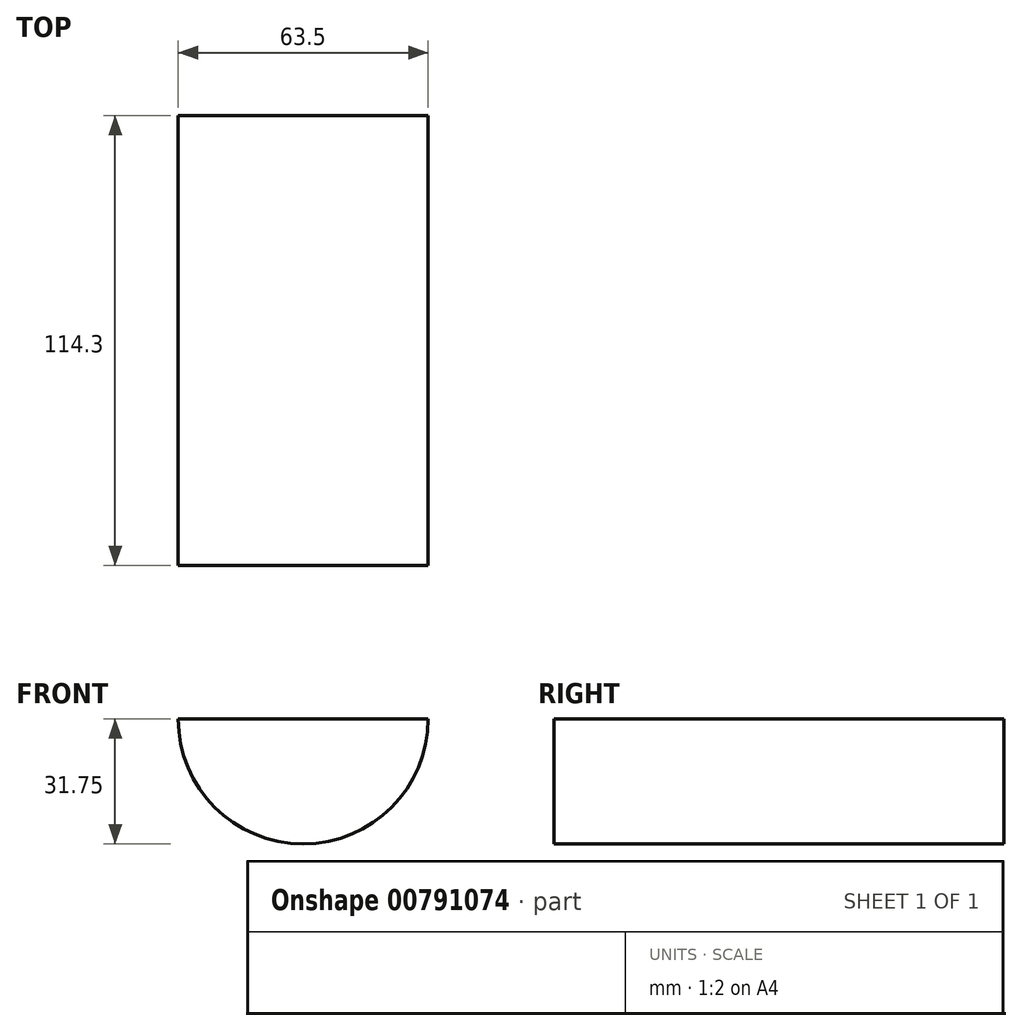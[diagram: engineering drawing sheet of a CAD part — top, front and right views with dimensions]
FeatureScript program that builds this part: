
annotation { "Feature Type Name" : "Feature", "Feature Type Description" : "" }
export const myFeature = defineFeature(function(context is Context, id is Id, definition is map)
    precondition{}
    {
        {
            var Q0;
            Q0=qCreatedBy(makeId("Front.planeOp"),FACE);
            var sketch = newSketch(context, id + "F0", { "sketchPlane" : qUnion([Q0])});
            skLineSegment(sketch, "E0", {"start": v(0, 0) * mm, "end": v(152.4, 0) * mm});
            skLineSegment(sketch, "E1", {"start": v(152.4, 0) * mm, "end": v(152.4, 92.08) * mm});
            skLineSegment(sketch, "E2", {"start": v(152.4, 92.08) * mm, "end": v(0, 92.08) * mm});
            skLineSegment(sketch, "E3", {"start": v(0, 92.08) * mm, "end": v(0, 0) * mm});
            skSolve(sketch);
        }
        {
            var Q0;
            Q0=makeQuery(id+"F0.imprint","IMPRINT",FACE,{"disambiguationData":[TD([[makeQuery(id+"F0.imprint","IMPRINT",EDGE,{"derivedFrom":sQuery(id+"F0.wireOp",EDGE,"E0")}),1.0]])]});
            extrude(context, id + "F1", {"entities" : qUnion([Q0]), "depth" : 114.3 * mm, "offsetDistance" : 25.4 * mm});
        }
        {
            var Q0;
            Q0=makeQuery(id+"F1.opExtrude","CAP_FACE",FACE,{"disambiguationData":[OSD([sQuery(id+"F0.wireOp",EDGE,"E0"),sQuery(id+"F0.wireOp",EDGE,"E1"),sQuery(id+"F0.wireOp",EDGE,"E2"),sQuery(id+"F0.wireOp",EDGE,"E3")])],"isStart":false});
            var sketch = newSketch(context, id + "F2", { "sketchPlane" : qUnion([Q0])});
            skLineSegment(sketch, "E4", {"start": v(152.4, 0) * mm, "end": v(152.4, 12.7) * mm});
            skLineSegment(sketch, "E5", {"start": v(152.4, 12.7) * mm, "end": v(114.3, 12.7) * mm});
            skLineSegment(sketch, "E6", {"start": v(114.3, 12.7) * mm, "end": v(114.3, 92.08) * mm});
            skLineSegment(sketch, "E7", {"start": v(0, 0) * mm, "end": v(0, 12.7) * mm});
            skLineSegment(sketch, "E8", {"start": v(0, 12.7) * mm, "end": v(38.1, 12.7) * mm});
            skLineSegment(sketch, "E9", {"start": v(38.1, 12.7) * mm, "end": v(38.1, 92.08) * mm});
            skSolve(sketch);
        }
        {
            var Q0;
            {var subQ0=sQuery(id+"F2.wireOp",EDGE,"E8");Q0=makeQuery(id+"F2.imprint","IMPRINT",FACE,{"disambiguationData":[TD([[makeQuery(id+"F2.imprint","IMPRINT",EDGE,{"derivedFrom":subQ0}),1.0]])]});}
            var Q1;
            {var subQ0=sQuery(id+"F2.wireOp",EDGE,"E5");Q1=makeQuery(id+"F2.imprint","IMPRINT",FACE,{"disambiguationData":[TD([[makeQuery(id+"F2.imprint","IMPRINT",EDGE,{"derivedFrom":subQ0}),-1.0]])]});}
            extrude(context, id + "F3", {"entities" : qUnion([Q0, Q1]), "operationType" : NewBodyOperationType.REMOVE, "oppositeDirection" : true, "depth" : 114.3 * mm, "offsetDistance" : 25.4 * mm});
        }
        {
            var Q0;
            Q0=makeQuery(id+"F1.opExtrude","CAP_FACE",FACE,{"disambiguationData":[OSD([sQuery(id+"F0.wireOp",EDGE,"E0"),sQuery(id+"F0.wireOp",EDGE,"E1"),sQuery(id+"F0.wireOp",EDGE,"E2"),sQuery(id+"F0.wireOp",EDGE,"E3")])],"isStart":false});
            var sketch = newSketch(context, id + "F4", { "sketchPlane" : qUnion([Q0])});
            skArc(sketch, "E10", {"start": v(107.95, 92.07) * mm, "mid": v(76.2, 60.33) * mm, "end": v(44.45, 92.08) * mm});
            skSolve(sketch);
        }
        {
            var Q0;
            {var subQ0=sQuery(id+"F4.wireOp",EDGE,"E10");Q0=makeQuery(id+"F4.imprint","IMPRINT",FACE,{"disambiguationData":[TD([[makeQuery(id+"F4.imprint","IMPRINT",EDGE,{"derivedFrom":subQ0}),-1.0]])]});}
            extrude(context, id + "F5", {"entities" : qUnion([Q0]), "operationType" : NewBodyOperationType.REMOVE, "oppositeDirection" : true, "depth" : 114.3 * mm, "offsetDistance" : 25.4 * mm});
        }
    });
